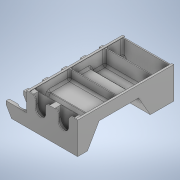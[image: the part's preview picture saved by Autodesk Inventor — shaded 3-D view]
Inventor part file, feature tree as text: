
AUTODESK INVENTOR PART (.ipt)
format: ipt  version: 2021 (Build 250183000, 183)  size: 587,776 bytes
history: native  units: mm
features: projected_geometry x15, extrude x14, sketch x12, pattern_linear x1, plane x1, fillet x1, chamfer x1
ambient origin geometry x8: Origin, YZ Plane, XZ Plane, XY Plane, X Axis, Y Axis, Z Axis, Center Point
bodies: Solid1 (feature_tree)
feature tree (45):
  sketch  "Sketch1"  dims[d0=101.0mm d1=61.0mm]
  extrude  "Extrusion1"  Depth=61.0mm
  extrude  "Extrusion2"  Depth=142.25mm
  extrude  "Extrusion3"  Depth=64.6mm TaperAngle=0.0deg
  sketch  "Sketch6"  dims[d5=44.8mm d6=64.6mm d7=0.0mm]
  extrude  "Extrusion5"  Depth=150.1mm
  extrude  "Extrusion6"  Depth=0.25mm
  pattern_linear  "Rectangular Pattern2"  Count1=3  [1 undecoded]
  extrude  "Extrusion8"  Depth=25.5mm
  extrude  "Extrusion9"  Depth=26.0mm
  extrude  "Extrusion12"  Depth=26.0mm TaperAngle=0.0deg
  sketch  "Sketch10"  dims[d16=11.0mm d17=0.0mm d43=25.5mm]
  plane  "Work Plane1"
  extrude  "Extrusion13"  Depth=26.0mm
  extrude  "Extrusion11"  TaperAngle=0.0deg  [1 undecoded]
  extrude  "Extrusion14"  Depth=112.166667mm
  fillet  "Fillet2"  Radius=30.083333mm
  extrude  "Extrusion16"  Depth=10.0mm
  extrude  "Extrusion17"  Depth=10.0mm
  extrude  "Extrusion18"  Depth=10.0mm
  chamfer  "Chamfer1"  Distance=7.866667mm
  sketch  "Sketch2"  dims[d2=2.0mm d4=142.25mm]
  projected_geometry  "Projected Loop1"
  projected_geometry  "Projected Loop4"
  sketch  "Sketch8"  dims[d8=11.0mm d9=0.0mm d10=150.1mm]
  projected_geometry  "Projected Loop7"
  sketch  "Sketch9"  dims[d11=108.4mm d12=0.25mm d15=30.0mm]
  projected_geometry  "Projected Loop8"
  projected_geometry  "Projected Loop9"
  projected_geometry  "Projected Loop10"
  sketch  "Sketch12"  dims[d44=2.041667mm d45=26.0mm]
  projected_geometry  "Projected Loop14"
  sketch  "Sketch13"  dims[d46=21.0mm d47=26.0mm d48=0.0mm]
  projected_geometry  "Projected Loop15"
  projected_geometry  "Projected Loop16"
  sketch  "Sketch14"  dims[d49=17.8mm d50=0.0mm d51=18.8mm d52=26.0mm]
  projected_geometry  "Projected Loop17"
  projected_geometry  "Projected Loop18"
  projected_geometry  "Projected Loop19"
  sketch  "Sketch15"  dims[d53=3.0mm d54=0.0mm d55=0.0mm]
  projected_geometry  "Projected Loop20"
  sketch  "Sketch16"  dims[d56=50.0mm d58=28.041667mm d59=112.166667mm d60=30.083333mm]
  projected_geometry  "Projected Loop21"
  sketch  "Sketch17"  dims[d61=28.041667mm d67=13.0mm d68=26.0mm d69=1.2mm d70=7.866667mm d71=7.866667mm d72=7.866667mm d73=8.0mm d74=27.0mm d75=0.0mm d76=4.0mm d77=15.0mm d78=26.0mm d79=0.0mm d80=14.75mm d91=13.75mm d92=0.0mm d96=135.0deg d97=0.0mm d98=0.0mm d99=1.2mm d100=1.6mm d101=1.6mm d102=1.6mm d103=1.2mm d104=1.2mm d105=25.0mm d106=51.425mm d107=1.0mm d108=1.2mm d109=1.6mm d110=10.0mm d111=0.0mm d112=15.872381mm d113=1.2mm d114=22.0mm d115=1.2mm d116=18.722381mm d117=10.0mm d118=0.0mm d121=3.0mm d122=1.0mm d123=12.0mm d124=2.0mm d125=1.5mm d126=9.272952mm d127=10.0mm d128=0.0mm d129=10.0mm d130=10.0mm d131=10.0mm d132=0.0mm d133=120.0deg d134=8.0mm d135=0.5mm d136=0.6mm d137=60.0deg d139=2.5mm d141=1.0mm d142=0.0mm d143=3.0mm d144=22.45mm d145=1.0mm d146=1.0mm d147=73.2mm d148=92.0mm d149=55.2mm d150=0.5mm d151=2.0mm d152=45.0deg]
  projected_geometry  "Projected Loop22"
note: 2 required parameter values undecoded (feature->parameter linkage not recoverable at this tier; creation-order binding heuristic only, values carry confidence <= 0.55)
